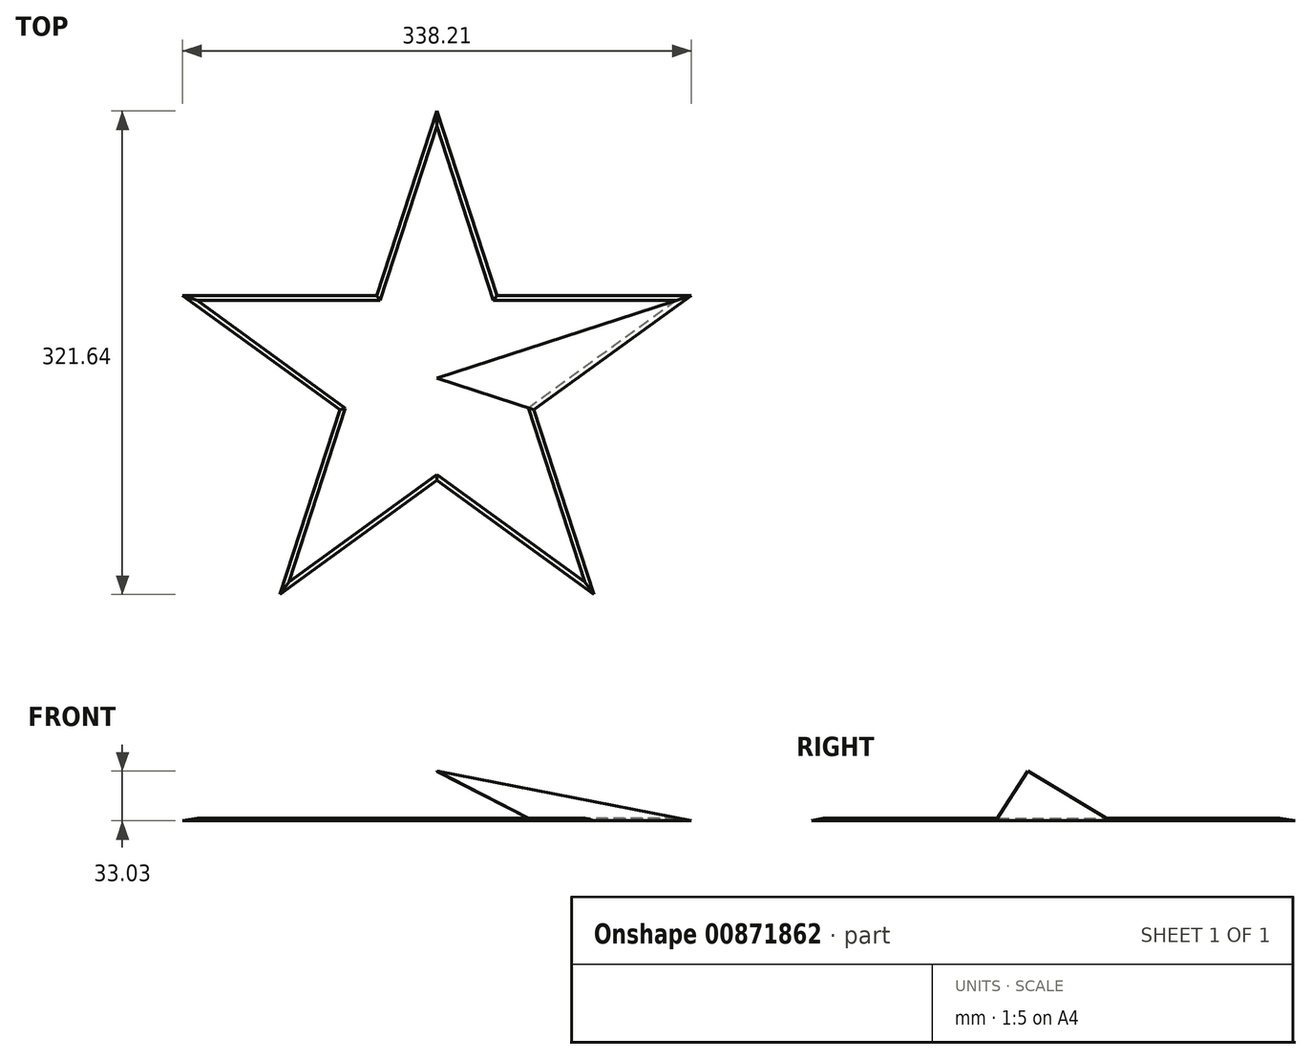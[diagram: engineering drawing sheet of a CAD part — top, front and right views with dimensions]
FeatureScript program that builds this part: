
annotation { "Feature Type Name" : "Feature", "Feature Type Description" : "" }
export const myFeature = defineFeature(function(context is Context, id is Id, definition is map)
    precondition{}
    {
        {
            assignVariable(context, id + "F0", {"name" : "diameter", "anyValue" : 14});
        }
        {
            assignVariable(context, id + "F1", {"name" : "height", "anyValue" : getVariable(context, 'diameter') / 7.4});
        }
        {
            var Q0;
            Q0=qCreatedBy(makeId("Top.planeOp"),FACE);
            var sketch = newSketch(context, id + "F2", { "sketchPlane" : qUnion([Q0])});
            skCircle(sketch, "E0", {"center": v(0, 0) * mm, "radius": 177.8 * mm, "construction": true});
            skPoint(sketch, "E1", {"position": v(0, 177.8) * mm});
            skPoint(sketch, "E2.1.0", {"position": v(-169.1, 54.94) * mm});
            skPoint(sketch, "E2.2.0", {"position": v(-104.5, -143.84) * mm});
            skPoint(sketch, "E2.3.0", {"position": v(104.5, -143.84) * mm});
            skPoint(sketch, "E2.4.0", {"position": v(169.1, 54.94) * mm});
            skSolve(sketch);
        }
        {
            var Q0;
            Q0=qCreatedBy(makeId("Top.planeOp"),FACE);
            var sketch = newSketch(context, id + "F3", { "sketchPlane" : qUnion([Q0])});
            skLineSegment(sketch, "E3", {"start": v(0, 177.8) * mm, "end": v(0, 0) * mm});
            skLineSegment(sketch, "E4", {"start": v(-169.1, 54.94) * mm, "end": v(-39.92, 54.94) * mm});
            skLineSegment(sketch, "E5", {"start": v(0, 0) * mm, "end": v(104.5, -143.84) * mm});
            skLineSegment(sketch, "E6", {"start": v(0, 0) * mm, "end": v(-104.5, -143.84) * mm});
            skLineSegment(sketch, "E7", {"start": v(0, 0) * mm, "end": v(169.1, 54.94) * mm});
            skLineSegment(sketch, "E8", {"start": v(0, 0) * mm, "end": v(-169.1, 54.94) * mm});
            skLineSegment(sketch, "E9", {"start": v(0, 177.8) * mm, "end": v(-39.92, 54.94) * mm});
            skLineSegment(sketch, "E10", {"start": v(0, 177.8) * mm, "end": v(39.92, 54.94) * mm});
            skLineSegment(sketch, "E11", {"start": v(-169.1, 54.94) * mm, "end": v(-64.59, -20.99) * mm});
            skLineSegment(sketch, "E12", {"start": v(169.1, 54.94) * mm, "end": v(64.59, -20.99) * mm});
            skLineSegment(sketch, "E13.trimOffspring", {"start": v(-64.59, -20.99) * mm, "end": v(-104.5, -143.84) * mm});
            skLineSegment(sketch, "E14.trimOffspring", {"start": v(0, -67.91) * mm, "end": v(104.5, -143.84) * mm});
            skLineSegment(sketch, "E15.trimOffspring", {"start": v(0, -67.91) * mm, "end": v(-104.5, -143.84) * mm});
            skLineSegment(sketch, "E16.trimOffspring", {"start": v(64.59, -20.99) * mm, "end": v(104.5, -143.84) * mm});
            skLineSegment(sketch, "E17.trimOffspring", {"start": v(39.92, 54.94) * mm, "end": v(169.1, 54.94) * mm});
            skLineSegment(sketch, "E18", {"start": v(0, 0) * mm, "end": v(-39.92, 54.94) * mm});
            skLineSegment(sketch, "E19", {"start": v(0, 0) * mm, "end": v(39.92, 54.94) * mm});
            skLineSegment(sketch, "E20", {"start": v(0, 0) * mm, "end": v(64.59, -20.99) * mm});
            skLineSegment(sketch, "E21", {"start": v(0, 0) * mm, "end": v(0, -67.91) * mm});
            skLineSegment(sketch, "E22", {"start": v(0, 0) * mm, "end": v(-64.59, -20.99) * mm});
            skSolve(sketch);
        }
        {
            var Q0;
            Q0 = qSketchRegion(id + "F3", true);
            extrude(context, id + "F4", {"entities" : qUnion([Q0]), "depth" : (getVariable(context, 'height')) * mm, "offsetDistance" : 25.4 * mm, "hasDraft" : true, "draftAngle" : 59 * degree, "draftPullDirection" : true});
        }
        {
            var Q0;
            Q0=makeQuery(id+"F4.opExtrude","SWEPT_FACE",FACE,{"disambiguationData":[OSD([sQuery(id+"F3.wireOp",EDGE,"E12")])]});
            var sketch = newSketch(context, id + "F5", { "sketchPlane" : qUnion([Q0])});
            skLineSegment(sketch, "E23.0.0", {"start": v(58.78, -18.87) * mm, "end": v(168.43, 49.41) * mm});
            skLineSegment(sketch, "E23.0.1", {"start": v(168.43, 49.41) * mm, "end": v(-8.99, 14.43) * mm});
            skLineSegment(sketch, "E23.0.2", {"start": v(-8.99, 14.43) * mm, "end": v(58.78, -18.87) * mm});
            skSolve(sketch);
        }
        {
            var Q0;
            Q0 = qSketchRegion(id + "F5", true);
            extrude(context, id + "F6", {"entities" : qUnion([Q0]), "depth" : 0.03 * mm, "offsetDistance" : 25.4 * mm});
        }
    });
